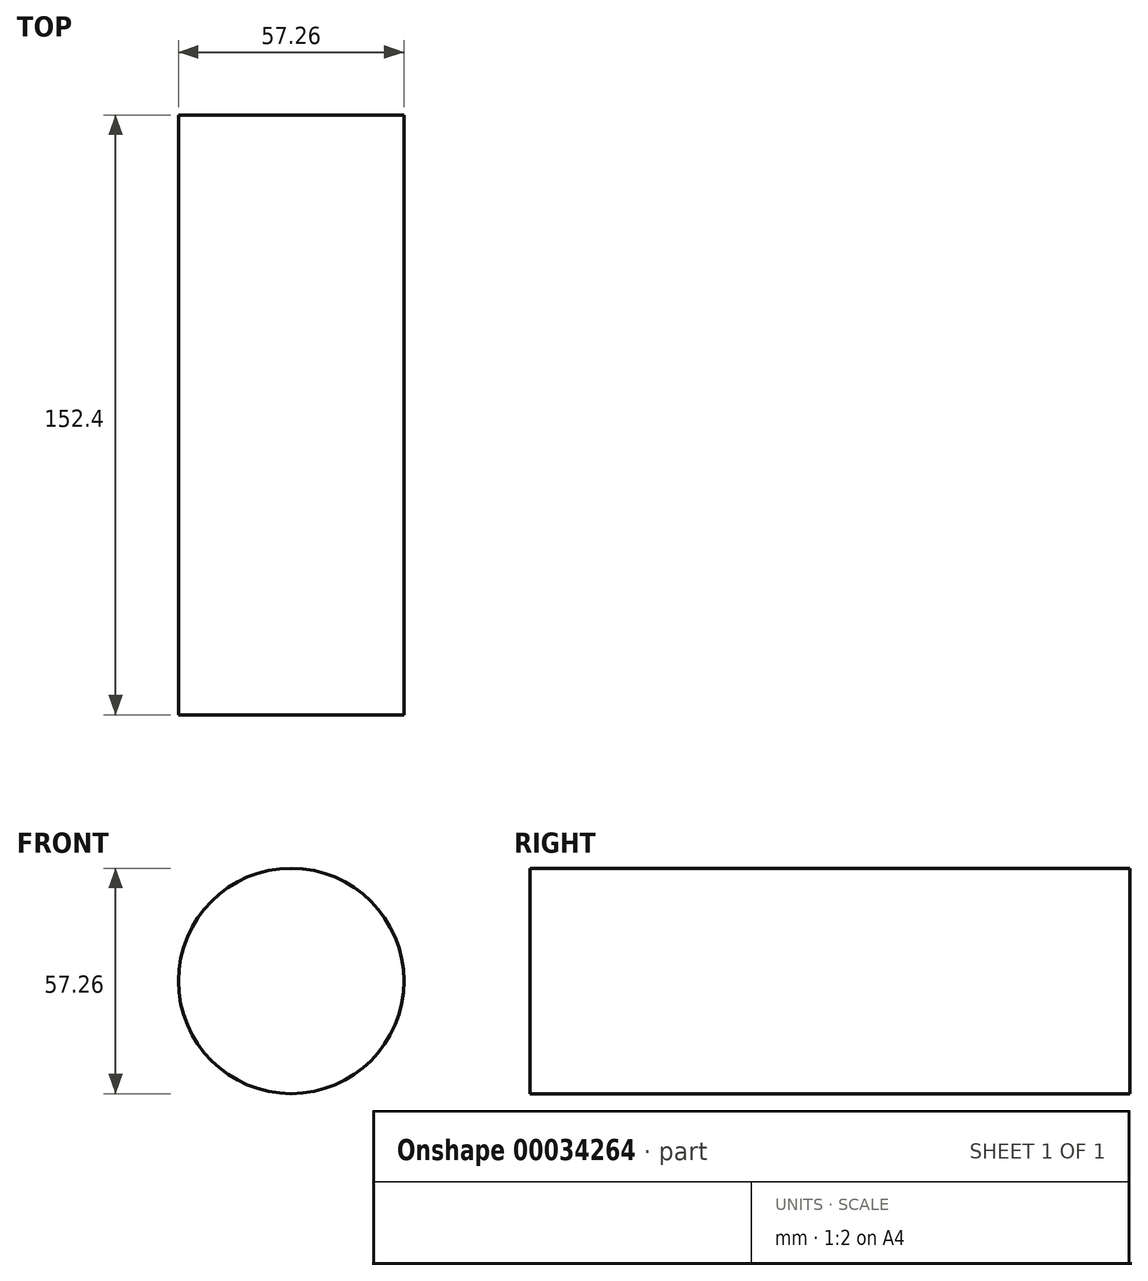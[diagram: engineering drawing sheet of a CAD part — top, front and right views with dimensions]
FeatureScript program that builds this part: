
annotation { "Feature Type Name" : "Feature", "Feature Type Description" : "" }
export const myFeature = defineFeature(function(context is Context, id is Id, definition is map)
    precondition{}
    {
        {
            var Q0;
            Q0=qCreatedBy(makeId("Front.planeOp"),FACE);
            var sketch = newSketch(context, id + "F0", { "sketchPlane" : qUnion([Q0])});
            skCircle(sketch, "E0", {"center": v(0, 0) * mm, "radius": 28.63 * mm});
            skSolve(sketch);
        }
        {
            var Q0;
            Q0=sQuery(id+"F0.wireOp",EDGE,"E0");
            extrude(context, id + "F1", {"bodyType" : ToolBodyType.SURFACE, "surfaceEntities" : qUnion([Q0]), "endBound" : BoundingType.SYMMETRIC, "depth" : 152.4 * mm});
        }
    });
